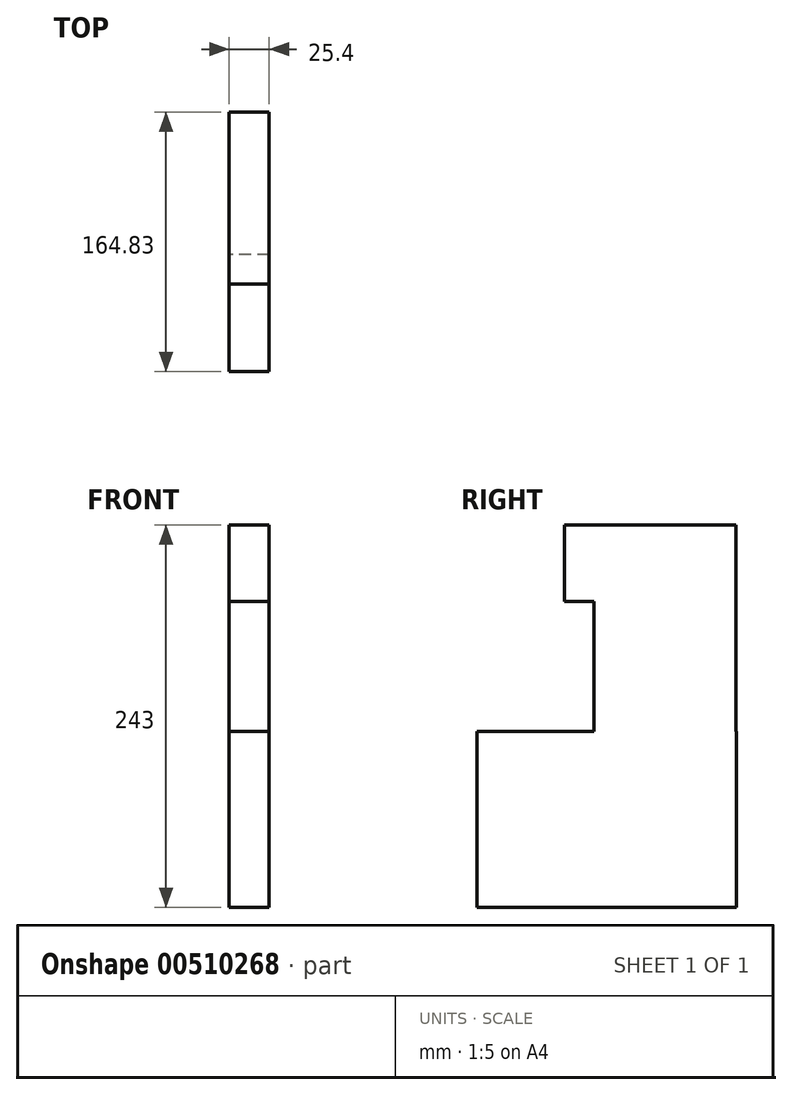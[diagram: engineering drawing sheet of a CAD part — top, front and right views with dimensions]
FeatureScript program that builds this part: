
annotation { "Feature Type Name" : "Feature", "Feature Type Description" : "" }
export const myFeature = defineFeature(function(context is Context, id is Id, definition is map)
    precondition{}
    {
        {
            var Q0;
            Q0=qCreatedBy(makeId("Right.planeOp"),FACE);
            var sketch = newSketch(context, id + "F0", { "sketchPlane" : qUnion([Q0])});
            skLineSegment(sketch, "E0.bottom", {"start": v(-126.86, 50.01) * mm, "end": v(37.97, 50.01) * mm});
            skLineSegment(sketch, "E0.top", {"start": v(-126.86, -61.84) * mm, "end": v(37.97, -61.84) * mm});
            skLineSegment(sketch, "E0.left", {"start": v(-126.86, 50.01) * mm, "end": v(-126.86, -61.84) * mm});
            skLineSegment(sketch, "E0.right", {"start": v(37.97, 50.01) * mm, "end": v(37.97, -61.84) * mm});
            skLineSegment(sketch, "E1.bottom", {"start": v(-52.52, 50.01) * mm, "end": v(37.84, 50.01) * mm});
            skLineSegment(sketch, "E1.top", {"start": v(-52.52, 132.7) * mm, "end": v(37.84, 132.7) * mm});
            skLineSegment(sketch, "E1.left", {"start": v(-52.52, 50.01) * mm, "end": v(-52.52, 132.7) * mm});
            skLineSegment(sketch, "E1.right", {"start": v(37.84, 50.01) * mm, "end": v(37.84, 132.7) * mm});
            skLineSegment(sketch, "E2.bottom", {"start": v(37.84, 132.7) * mm, "end": v(-71.23, 132.7) * mm});
            skLineSegment(sketch, "E2.top", {"start": v(37.84, 181.16) * mm, "end": v(-71.23, 181.16) * mm});
            skLineSegment(sketch, "E2.left", {"start": v(37.84, 132.7) * mm, "end": v(37.84, 181.16) * mm});
            skLineSegment(sketch, "E2.right", {"start": v(-71.23, 132.7) * mm, "end": v(-71.23, 181.16) * mm});
            skSolve(sketch);
        }
        {
            var Q0;
            Q0 = qSketchRegion(id + "F0", true);
            extrude(context, id + "F1", {"entities" : qUnion([Q0]), "depth" : 25.4 * mm});
        }
    });
